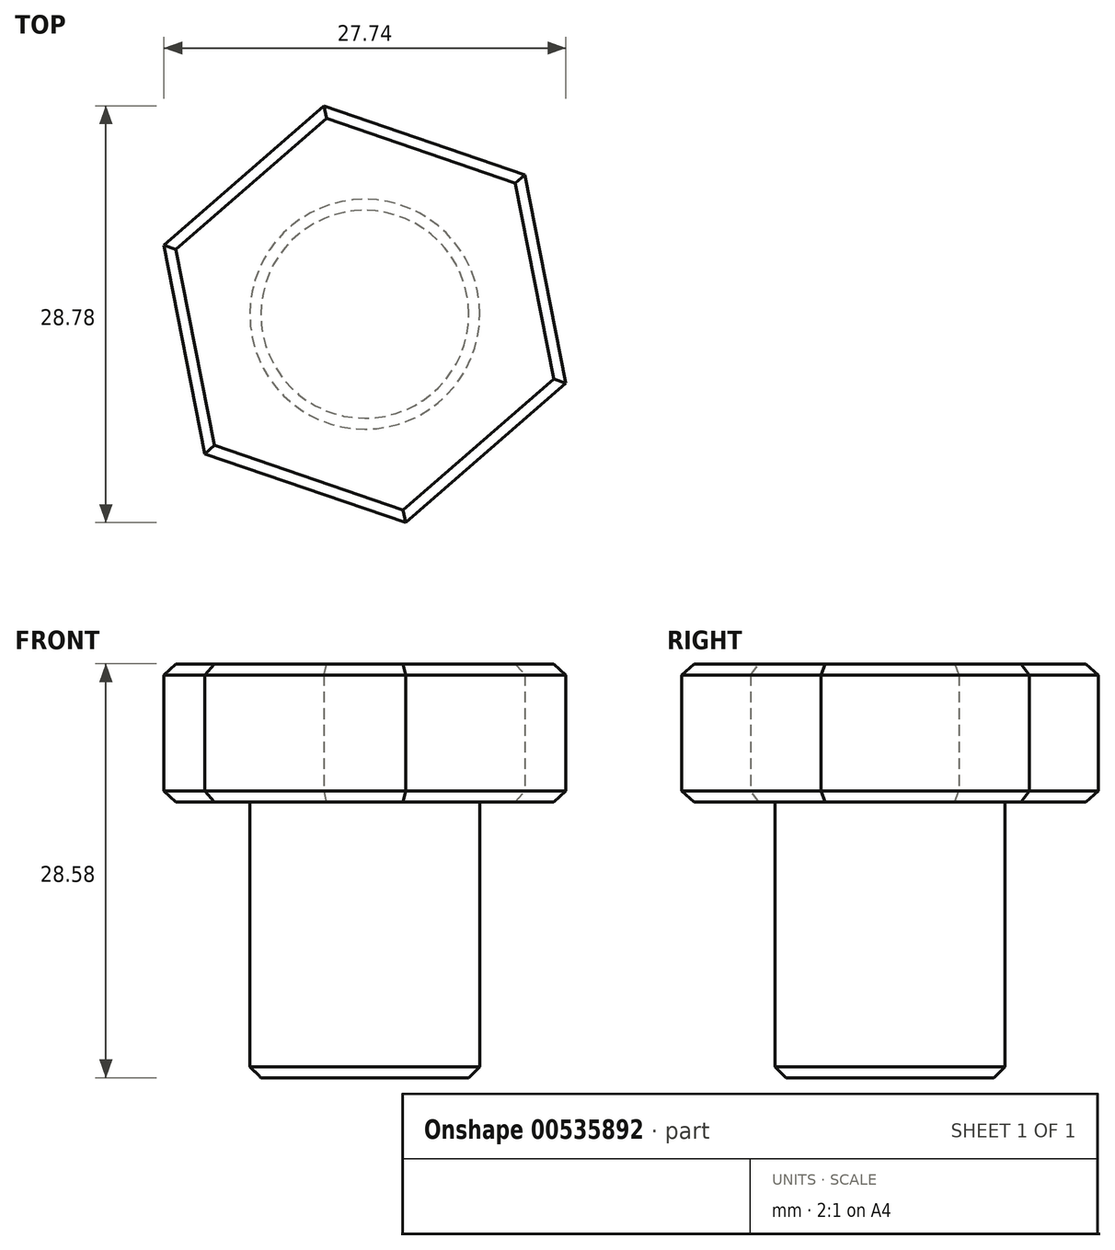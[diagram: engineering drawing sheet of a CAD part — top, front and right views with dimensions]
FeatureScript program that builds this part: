
annotation { "Feature Type Name" : "Feature", "Feature Type Description" : "" }
export const myFeature = defineFeature(function(context is Context, id is Id, definition is map)
    precondition{}
    {
        {
            var Q0;
            Q0=qCreatedBy(makeId("Top.planeOp"),FACE);
            var sketch = newSketch(context, id + "F0", { "sketchPlane" : qUnion([Q0])});
            skCircle(sketch, "E0", {"center": v(0, 0) * mm, "radius": 12.7 * mm});
            skCircle(sketch, "E1.cCircle", {"center": v(0, 0) * mm, "radius": 12.7 * mm, "construction": true});
            skLineSegment(sketch, "E1.0", {"start": v(-13.87, 4.76) * mm, "end": v(-2.81, 14.4) * mm});
            skLineSegment(sketch, "E1.1", {"start": v(-2.81, 14.4) * mm, "end": v(11.06, 9.63) * mm});
            skLineSegment(sketch, "E1.2", {"start": v(11.06, 9.63) * mm, "end": v(13.87, -4.76) * mm});
            skLineSegment(sketch, "E1.3", {"start": v(13.87, -4.76) * mm, "end": v(2.81, -14.4) * mm});
            skLineSegment(sketch, "E1.4", {"start": v(2.81, -14.4) * mm, "end": v(-11.06, -9.63) * mm});
            skLineSegment(sketch, "E1.5", {"start": v(-11.06, -9.63) * mm, "end": v(-13.87, 4.76) * mm});
            skPoint(sketch, "E1.0.midPoint", {"position": v(-8.34, 9.58) * mm});
            skSolve(sketch);
        }
        {
            var Q0;
            {var subQ0=sQuery(id+"F0.wireOp",EDGE,"E1.2");var subQ1=sQuery(id+"F0.wireOp",EDGE,"E0");var subQ2=makeQuery(id+"F0.imprint","INTERSECT",VERTEX,{"derivedFrom":[subQ1,subQ0]});Q0=makeQuery(id+"F0.imprint","IMPRINT",FACE,{"disambiguationData":[TD([[makeQuery(id+"F0.imprint","IMPRINT",EDGE,{"disambiguationData":[TD([[subQ2,1.0]])],"derivedFrom":subQ1}),-1.0]])]});}
            var Q1;
            {var subQ0=sQuery(id+"F0.wireOp",EDGE,"E1.4");var subQ1=sQuery(id+"F0.wireOp",EDGE,"E0");var subQ2=makeQuery(id+"F0.imprint","INTERSECT",VERTEX,{"derivedFrom":[subQ1,subQ0]});Q1=makeQuery(id+"F0.imprint","IMPRINT",FACE,{"disambiguationData":[TD([[makeQuery(id+"F0.imprint","IMPRINT",EDGE,{"disambiguationData":[TD([[subQ2,-1.0]])],"derivedFrom":subQ1}),-1.0]])]});}
            var Q2;
            {var subQ0=sQuery(id+"F0.wireOp",EDGE,"E1.1");var subQ1=sQuery(id+"F0.wireOp",EDGE,"E0");var subQ2=makeQuery(id+"F0.imprint","INTERSECT",VERTEX,{"derivedFrom":[subQ1,subQ0]});Q2=makeQuery(id+"F0.imprint","IMPRINT",FACE,{"disambiguationData":[TD([[makeQuery(id+"F0.imprint","IMPRINT",EDGE,{"disambiguationData":[TD([[subQ2,1.0]])],"derivedFrom":subQ1}),-1.0]])]});}
            var Q3;
            {var subQ0=sQuery(id+"F0.wireOp",EDGE,"E1.0");var subQ1=sQuery(id+"F0.wireOp",EDGE,"E0");var subQ2=makeQuery(id+"F0.imprint","INTERSECT",VERTEX,{"derivedFrom":[subQ1,subQ0]});Q3=makeQuery(id+"F0.imprint","IMPRINT",FACE,{"disambiguationData":[TD([[makeQuery(id+"F0.imprint","IMPRINT",EDGE,{"disambiguationData":[TD([[subQ2,-1.0]])],"derivedFrom":subQ1}),-1.0]])]});}
            var Q4;
            {var subQ0=sQuery(id+"F0.wireOp",EDGE,"E1.5");var subQ1=sQuery(id+"F0.wireOp",EDGE,"E0");var subQ2=makeQuery(id+"F0.imprint","INTERSECT",VERTEX,{"derivedFrom":[subQ1,subQ0]});Q4=makeQuery(id+"F0.imprint","IMPRINT",FACE,{"disambiguationData":[TD([[makeQuery(id+"F0.imprint","IMPRINT",EDGE,{"disambiguationData":[TD([[subQ2,-1.0]])],"derivedFrom":subQ1}),-1.0]])]});}
            var Q5;
            {var subQ0=sQuery(id+"F0.wireOp",EDGE,"E1.1");var subQ1=sQuery(id+"F0.wireOp",EDGE,"E0");var subQ2=makeQuery(id+"F0.imprint","INTERSECT",VERTEX,{"derivedFrom":[subQ1,subQ0]});Q5=makeQuery(id+"F0.imprint","IMPRINT",FACE,{"disambiguationData":[TD([[makeQuery(id+"F0.imprint","IMPRINT",EDGE,{"disambiguationData":[TD([[subQ2,-1.0]])],"derivedFrom":subQ1}),-1.0]])]});}
            var Q6;
            {var subQ0=sQuery(id+"F0.wireOp",EDGE,"E0");var subQ4=makeQuery(id+"F0.imprint","INTERSECT",VERTEX,{"derivedFrom":[subQ0,sQuery(id+"F0.wireOp",EDGE,"E1.1")]});Q6=makeQuery(id+"F0.imprint","IMPRINT",FACE,{"disambiguationData":[TD([[makeQuery(id+"F0.imprint","IMPRINT",EDGE,{"disambiguationData":[TD([[subQ4,1.0]])],"derivedFrom":subQ0}),1.0]])]});}
            extrude(context, id + "F1", {"entities" : qUnion([Q0, Q1, Q2, Q3, Q4, Q5, Q6]), "depth" : 9.52 * mm, "offsetDistance" : 25.4 * mm});
        }
        {
            var Q0;
            Q0=makeQuery(id+"F1.opExtrude","CAP_FACE",FACE,{"disambiguationData":[OSD([sQuery(id+"F0.wireOp",EDGE,"E1.0"),sQuery(id+"F0.wireOp",EDGE,"E1.1"),sQuery(id+"F0.wireOp",EDGE,"E1.2"),sQuery(id+"F0.wireOp",EDGE,"E1.3"),sQuery(id+"F0.wireOp",EDGE,"E1.4"),sQuery(id+"F0.wireOp",EDGE,"E1.5")])],"isStart":true});
            var sketch = newSketch(context, id + "F2", { "sketchPlane" : qUnion([Q0])});
            skCircle(sketch, "E2", {"center": v(0, 0) * mm, "radius": 7.94 * mm});
            skSolve(sketch);
        }
        {
            var Q0;
            Q0=makeQuery(id+"F2.imprint","IMPRINT",FACE,{"disambiguationData":[TD([[makeQuery(id+"F2.imprint","IMPRINT",EDGE,{"derivedFrom":sQuery(id+"F2.wireOp",EDGE,"E2")}),1.0]])]});
            extrude(context, id + "F3", {"entities" : qUnion([Q0]), "operationType" : NewBodyOperationType.ADD, "depth" : 19.05 * mm, "offsetDistance" : 25.4 * mm});
        }
        {
            var Q0;
            Q0=makeQuery(id+"F1.opExtrude","CAP_EDGE",EDGE,{"disambiguationData":[OSD([sQuery(id+"F0.wireOp",EDGE,"E1.1")])],"isStart":false});
            var Q1;
            Q1=makeQuery(id+"F1.opExtrude","CAP_EDGE",EDGE,{"disambiguationData":[OSD([sQuery(id+"F0.wireOp",EDGE,"E1.2")])],"isStart":false});
            var Q2;
            Q2=makeQuery(id+"F1.opExtrude","CAP_EDGE",EDGE,{"disambiguationData":[OSD([sQuery(id+"F0.wireOp",EDGE,"E1.3")])],"isStart":false});
            var Q3;
            Q3=makeQuery(id+"F1.opExtrude","CAP_EDGE",EDGE,{"disambiguationData":[OSD([sQuery(id+"F0.wireOp",EDGE,"E1.5")])],"isStart":false});
            var Q4;
            Q4=makeQuery(id+"F1.opExtrude","CAP_EDGE",EDGE,{"disambiguationData":[OSD([sQuery(id+"F0.wireOp",EDGE,"E1.4")])],"isStart":false});
            var Q5;
            Q5=makeQuery(id+"F1.opExtrude","CAP_EDGE",EDGE,{"disambiguationData":[OSD([sQuery(id+"F0.wireOp",EDGE,"E1.0")])],"isStart":false});
            var Q6;
            Q6=makeQuery(id+"F3.opExtrude","CAP_EDGE",EDGE,{"disambiguationData":[OSD([sQuery(id+"F2.wireOp",EDGE,"E2")])],"isStart":false});
            var Q7;
            Q7=makeQuery(id+"F1.opExtrude","CAP_EDGE",EDGE,{"disambiguationData":[OSD([sQuery(id+"F0.wireOp",EDGE,"E1.3")])],"isStart":true});
            var Q8;
            Q8=makeQuery(id+"F1.opExtrude","CAP_EDGE",EDGE,{"disambiguationData":[OSD([sQuery(id+"F0.wireOp",EDGE,"E1.2")])],"isStart":true});
            var Q9;
            Q9=makeQuery(id+"F1.opExtrude","CAP_EDGE",EDGE,{"disambiguationData":[OSD([sQuery(id+"F0.wireOp",EDGE,"E1.1")])],"isStart":true});
            var Q10;
            Q10=makeQuery(id+"F1.opExtrude","CAP_EDGE",EDGE,{"disambiguationData":[OSD([sQuery(id+"F0.wireOp",EDGE,"E1.0")])],"isStart":true});
            var Q11;
            Q11=makeQuery(id+"F1.opExtrude","CAP_EDGE",EDGE,{"disambiguationData":[OSD([sQuery(id+"F0.wireOp",EDGE,"E1.5")])],"isStart":true});
            var Q12;
            Q12=makeQuery(id+"F1.opExtrude","CAP_EDGE",EDGE,{"disambiguationData":[OSD([sQuery(id+"F0.wireOp",EDGE,"E1.4")])],"isStart":true});
            chamfer(context, id + "F4", {"entities" : qUnion([Q0, Q1, Q2, Q3, Q4, Q5, Q6, Q7, Q8, Q9, Q10, Q11, Q12]), "chamferType" : ChamferType.OFFSET_ANGLE, "width" : 0.76 * mm, "oppositeDirection" : false, "angle" : 45 * degree, "tangentPropagation" : true});
        }
    });
